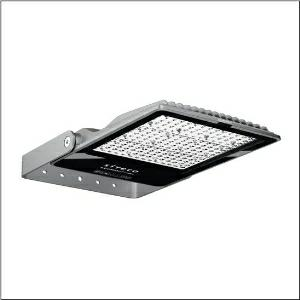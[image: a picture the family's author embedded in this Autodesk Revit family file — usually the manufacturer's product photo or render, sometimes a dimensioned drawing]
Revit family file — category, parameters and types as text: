
# Revit family: sicompact_r__31_midi___pl32_5xa7581d2k23_8dbf
name_source: partatom
category: Lighting Fixtures
units: mm (PartAtom-declared; Revit-internal decimal feet)

## family parameters
Cut with Voids When Loaded = No
Host = Face
Light Source = No
Part Type = Normal
Room Calculation Point = No
Round Connector Dimension = Use Diameter
Shared = No

## types (1)
- SiCompact® 31 midi  PL32 (1 x LED, 27000 lm, 165 W, 4000K)
    Apparent Load = 165 VA
    CIE Flux Codes = 32 69 98 100 100
    Color Rendering = 70
    Color Temperature = 4000K
    Default Elevation = 1800 mm
    Description = SiCompact® 31 midi, floodlight, primary light control with lens, of plastic, of toughened safety glass, transparent, light distribution: PL32, light emission: direct distribution, primary light characteristic: asymmetric, installation type: surface-mounted, LED, High Power LED, rated luminous flux: 27.000lm, luminous efficacy: 164lm/W, light colour: 740, colour temperature: 4000K, control gear: ON/OFF, with cable, 3x 1.5mm², mains connection: 220..240V, AC, 50/60Hz, connection cable pre-assembled, cable length: 2m, rated input power: 165W, of diecast aluminium, specular, metallic grey (RAL 9006), length: 560mm, width: 330mm, height: 62mm, bracket, of sheet steel, coated, metallic grey (RAL 9006), ON/OFF, protection rating (complete): IP66, insulation class (complete): insulation class I (protective earthing), certification: CE, ENEC, impact resistance: IK08, permissible operating ambient temperature: -40..+45°C, packaging unit: 1 piece

Light Distribution: PL32
    Height = 62 mm  [stored 0.203412 ft]
    Lamp = 1 x LED
    Lamp Light Flux = 27000 lm
    Lamp Power = 165 W
    Lamp count = 1
    Length = 560 mm
    Luminous efficacy = 164 lm/W
    Manufacturer = Siteco
    ModVariant = No
    Model = 5XA7581D2K23
    Mounting Place = Wall
    Mounting Type = Surface mounted
    Number of Poles = 1
    OnlyDefault = Yes
    Power Factor = 1
    Product Name = SiCompact® 31 midi | PL32
    Product group = floodlight | wall mounted
    ProductGroupID = 2001
    Protection Class = Protection class I
    Protection Degree = IP 66
    RLX_Detail_Level = 1
    RLX_Emergency_Light_Flux = 0 lm
    RLX_Emergency_Type = 0
    RLX_Emergency_Type_DB = No
    RlxData = <blob elided: 98137 chars, md5=41cc18de>
    Socket = socket
    Standby Power = 0 W
    System Light Flux = 27000 lm
    System Power = 165 W
    Type Comments = Product without accessories
    Type Image = l_1006415.jpg
    URL = http://relux.com
    VarID = ---
    Voltage = 0 V
    Weight = 0.00 kg
    Width = 333 mm

note: [stored X ft] marks values corroborated as IEEE doubles in the binary element streams (Revit-internal decimal feet)

## geometry (parser evidence)
native form markers: Blend x4, Sweep x12
no freeform markers — native parametric forms only
